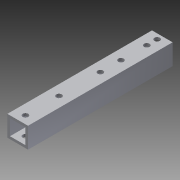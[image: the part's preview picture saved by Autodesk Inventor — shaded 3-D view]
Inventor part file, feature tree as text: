
AUTODESK INVENTOR PART (.ipt)
format: ipt  version: 2013 (Build 170138000, 138)  size: 114,176 bytes
history: native  units: in
note: dims shown in document units (in); Inventor stores cm internally (conversion verified against a paired STEP export)
features: reference x7, extrude x4, sketch x4
ambient origin geometry x8: Origin, YZ Plane, XZ Plane, XY Plane, X Axis, Y Axis, Z Axis, Center Point
bodies: Solid1 (feature_tree)
feature tree (15):
  extrude  "Extrusion1"  Depth=1.0in
  extrude  "Extrusion2"  Depth=7.0in TaperAngle=0.0deg
  extrude  "Extrusion3"  Depth=1.0in TaperAngle=0.0deg
  extrude  "Extrusion4"  [1 undecoded]
  sketch  "Sketch1"  dims[d0=1.0in d2=1.0in]
  sketch  "Sketch2"  dims[d3=0.125in d4=7.0in d5=0.0in]
  reference  "Reference1"
  reference  "Reference2"
  sketch  "Sketch3"  dims[d6=1.0in d7=0.0in d8=1.0in d9=0.0in]
  reference  "Reference3"
  reference  "Reference4"
  reference  "Reference5"
  sketch  "Sketch5"  dims[d10=1.0in d11=0.0in]
  reference  "Reference6"
  reference  "Reference7"
note: 1 required parameter value undecoded (feature->parameter linkage not recoverable at this tier; creation-order binding heuristic only, values carry confidence <= 0.55)
